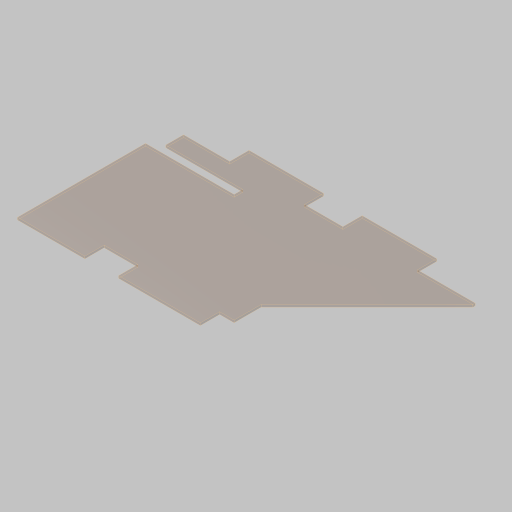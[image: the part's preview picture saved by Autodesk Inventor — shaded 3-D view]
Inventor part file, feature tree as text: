
AUTODESK INVENTOR PART (.ipt)
format: ipt  version: 2023.5 (Build 275446000, 446)  size: 255,488 bytes
history: native  units: in
note: dims shown in document units (in); Inventor stores cm internally (conversion verified against a paired STEP export)
features: sketch x5, other x3, projected_geometry x3, sheet_metal_op x1, extrude x1
ambient origin geometry x8: Origin, YZ Plane, XZ Plane, XY Plane, X Axis, Y Axis, Z Axis, Center Point
bodies: Solid1 (feature_tree)
feature tree (13):
  sheet_metal_op  "Face1"
  sketch  "Sketch3"  dims[d2=0.12in]
  extrude  "Extrusion1"  Depth=28.0in
  sketch  "Sketch1"  dims[d0=18.5in d1=28.0in]
  other  "Plate1"
  sketch  "Sketch4"  dims[d3=8.25in]
  projected_geometry  "Projected Loop1"
  sketch  "Sketch5"  dims[d4=10.0in]
  sketch  "Sketch6"  dims[d5=45.0deg d6=2.4in d9=2.75in d10=0.12in d11=0.0in d12=45.0deg d13=8.25in d14=9.0in d15=2.75in d16=2.4in d17=6.75in d18=4.5in d19=0.25in d21=4.0in d22=1.0in d23=0.1in d26=5.7in d31=0.5in d32=4.5in d33=6.75in d34=0.25in d35=4.0in d36=1.0in d37=0.1in d38=3.0in d39=1.4in d40=1.7in d41=0.1in d42=1.0in d43=0.75in d44=1.0in d45=0.75in d46=0.75in d47=1.0in d48=0.75in d49=1.0in d50=0.12in d51=0.0in d52=1.75in d53=1.0in d54=3.5in d55=1.75in d56=1.0in d57=3.5in d58=1.0in d59=0.125in d60=3.0in d61=2.0in d62=11.0in d63=1.0in d64=0.0in]
  other  "Cut1"
  other  "Cut2"
  projected_geometry  "Project Cut Edges1"
  projected_geometry  "Project Cut Edges2"
